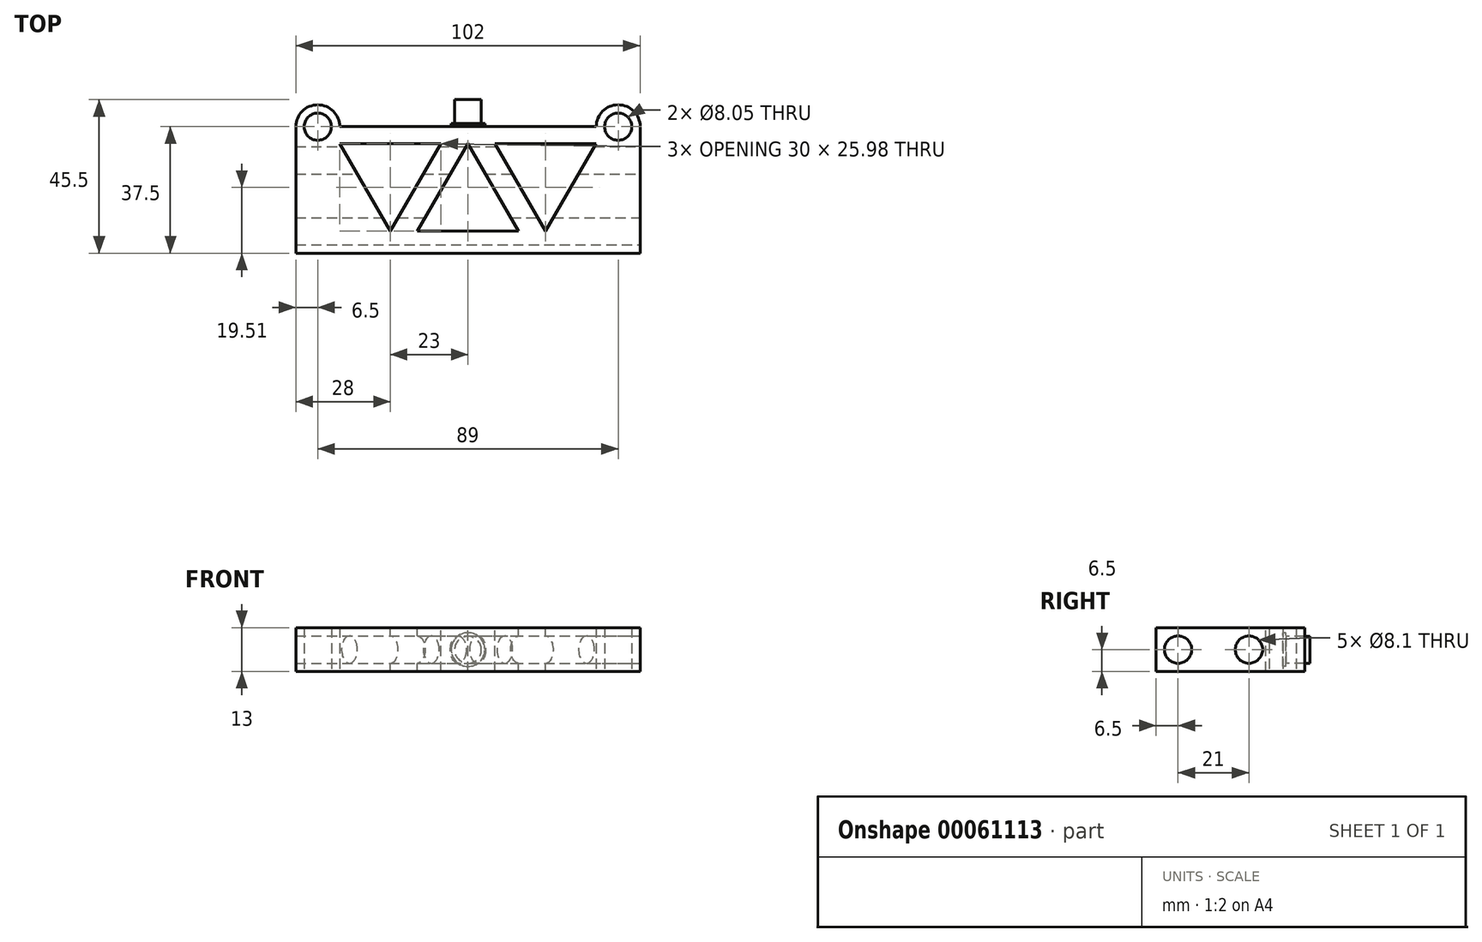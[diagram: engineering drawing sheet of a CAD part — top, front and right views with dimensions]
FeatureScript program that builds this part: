
annotation { "Feature Type Name" : "Feature", "Feature Type Description" : "" }
export const myFeature = defineFeature(function(context is Context, id is Id, definition is map)
    precondition{}
    {
        {
            var Q0;
            Q0=qCreatedBy(makeId("Top.planeOp"),FACE);
            var sketch = newSketch(context, id + "F0", { "sketchPlane" : qUnion([Q0])});
            skLineSegment(sketch, "E0", {"start": v(0, 0) * mm, "end": v(-38, 0) * mm});
            skLineSegment(sketch, "E1", {"start": v(0, 0) * mm, "end": v(38, 0) * mm});
            skCircle(sketch, "E2", {"center": v(-44.5, 0) * mm, "radius": 4.03 * mm});
            skCircle(sketch, "E3", {"center": v(44.5, 0) * mm, "radius": 4.03 * mm});
            skArc(sketch, "E4", {"start": v(-38, 0) * mm, "mid": v(-44.5, 6.5) * mm, "end": v(-51, 0) * mm});
            skArc(sketch, "E5", {"start": v(51, 0) * mm, "mid": v(44.5, 6.5) * mm, "end": v(38, 0) * mm});
            skLineSegment(sketch, "E6", {"start": v(0, 0) * mm, "end": v(0, -37.5) * mm, "construction": true});
            skLineSegment(sketch, "E7", {"start": v(0, -37.5) * mm, "end": v(-51, -37.5) * mm});
            skLineSegment(sketch, "E8", {"start": v(0, -37.5) * mm, "end": v(51, -37.5) * mm});
            skLineSegment(sketch, "E9", {"start": v(-51, -37.5) * mm, "end": v(-51, 0) * mm});
            skLineSegment(sketch, "E10", {"start": v(51, -37.5) * mm, "end": v(51, 0) * mm});
            skSolve(sketch);
        }
        {
            var Q0;
            Q0=makeQuery(id+"F0.imprint","IMPRINT",FACE,{"disambiguationData":[TD([[makeQuery(id+"F0.imprint","IMPRINT",EDGE,{"derivedFrom":sQuery(id+"F0.wireOp",EDGE,"E0")}),1.0]])]});
            extrude(context, id + "F1", {"entities" : qUnion([Q0]), "depth" : 13 * mm});
        }
        {
            var Q0;
            Q0=makeQuery(id+"F1.opExtrude","SWEPT_FACE",FACE,{"disambiguationData":[OSD([sQuery(id+"F0.wireOp",EDGE,"E10")])]});
            var sketch = newSketch(context, id + "F2", { "sketchPlane" : qUnion([Q0])});
            skLineSegment(sketch, "E11", {"start": v(0, 6.5) * mm, "end": v(-10, 6.5) * mm, "construction": true});
            skCircle(sketch, "E12", {"center": v(-10, 6.5) * mm, "radius": 4.05 * mm});
            skLineSegment(sketch, "E13", {"start": v(-10, 6.5) * mm, "end": v(-31, 6.5) * mm, "construction": true});
            skCircle(sketch, "E14", {"center": v(-31, 6.5) * mm, "radius": 4.05 * mm});
            skSolve(sketch);
        }
        {
            var Q0;
            Q0=makeQuery(id+"F2.imprint","IMPRINT",FACE,{"disambiguationData":[TD([[makeQuery(id+"F2.imprint","IMPRINT",EDGE,{"derivedFrom":sQuery(id+"F2.wireOp",EDGE,"E12")}),1.0]])]});
            var Q1;
            Q1=makeQuery(id+"F2.imprint","IMPRINT",FACE,{"disambiguationData":[TD([[makeQuery(id+"F2.imprint","IMPRINT",EDGE,{"derivedFrom":sQuery(id+"F2.wireOp",EDGE,"E14")}),1.0]])]});
            extrude(context, id + "F3", {"entities" : qUnion([Q0, Q1]), "operationType" : NewBodyOperationType.REMOVE, "oppositeDirection" : true, "depth" : 200 * mm});
        }
        {
            var Q0;
            Q0=makeQuery(id+"F1.opExtrude","CAP_FACE",FACE,{"disambiguationData":[OSD([sQuery(id+"F0.wireOp",EDGE,"E0"),sQuery(id+"F0.wireOp",EDGE,"E1"),sQuery(id+"F0.wireOp",EDGE,"E2"),sQuery(id+"F0.wireOp",EDGE,"E3"),sQuery(id+"F0.wireOp",EDGE,"E4"),sQuery(id+"F0.wireOp",EDGE,"E5"),sQuery(id+"F0.wireOp",EDGE,"E7"),sQuery(id+"F0.wireOp",EDGE,"E8"),sQuery(id+"F0.wireOp",EDGE,"E9"),sQuery(id+"F0.wireOp",EDGE,"E10")])],"isStart":false});
            var sketch = newSketch(context, id + "F4", { "sketchPlane" : qUnion([Q0])});
            skLineSegment(sketch, "E15", {"start": v(-8, -5) * mm, "end": v(-38, -5) * mm});
            skLineSegment(sketch, "E16", {"start": v(-38, -5) * mm, "end": v(-23, -30.98) * mm});
            skLineSegment(sketch, "E17", {"start": v(-23, -30.98) * mm, "end": v(-8, -5) * mm});
            skLineSegment(sketch, "E18", {"start": v(-38, 0) * mm, "end": v(-38, -5) * mm, "construction": true});
            skLineSegment(sketch, "E19", {"start": v(38, 0) * mm, "end": v(38, -5) * mm, "construction": true});
            skLineSegment(sketch, "E20", {"start": v(38, -5) * mm, "end": v(8, -5) * mm});
            skLineSegment(sketch, "E21", {"start": v(8, -5) * mm, "end": v(23, -30.98) * mm});
            skLineSegment(sketch, "E22", {"start": v(23, -30.98) * mm, "end": v(38, -5) * mm});
            skLineSegment(sketch, "E23", {"start": v(0, -5) * mm, "end": v(-15, -30.98) * mm});
            skLineSegment(sketch, "E24", {"start": v(-15, -30.98) * mm, "end": v(15, -30.98) * mm});
            skLineSegment(sketch, "E25", {"start": v(15, -30.98) * mm, "end": v(0, -5) * mm});
            skSolve(sketch);
        }
        {
            var Q0;
            Q0=makeQuery(id+"F4.imprint","IMPRINT",FACE,{"disambiguationData":[TD([[makeQuery(id+"F4.imprint","IMPRINT",EDGE,{"derivedFrom":sQuery(id+"F4.wireOp",EDGE,"E15")}),1.0]])]});
            var Q1;
            Q1=makeQuery(id+"F4.imprint","IMPRINT",FACE,{"disambiguationData":[TD([[makeQuery(id+"F4.imprint","IMPRINT",EDGE,{"derivedFrom":sQuery(id+"F4.wireOp",EDGE,"E23")}),1.0]])]});
            var Q2;
            Q2=makeQuery(id+"F4.imprint","IMPRINT",FACE,{"disambiguationData":[TD([[makeQuery(id+"F4.imprint","IMPRINT",EDGE,{"derivedFrom":sQuery(id+"F4.wireOp",EDGE,"E20")}),1.0]])]});
            extrude(context, id + "F5", {"entities" : qUnion([Q0, Q1, Q2]), "operationType" : NewBodyOperationType.REMOVE, "oppositeDirection" : true, "depth" : 25 * mm});
        }
        {
            var Q0;
            Q0=makeQuery(id+"F1.opExtrude","SWEPT_FACE",FACE,{"disambiguationData":[OSD([sQuery(id+"F0.wireOp",EDGE,"E0"),sQuery(id+"F0.wireOp",EDGE,"E1")])]});
            var sketch = newSketch(context, id + "F6", { "sketchPlane" : qUnion([Q0])});
            skLineSegment(sketch, "E26", {"start": v(0, 0) * mm, "end": v(0, 6.5) * mm, "construction": true});
            skCircle(sketch, "E27", {"center": v(0, 6.5) * mm, "radius": 5 * mm});
            skCircle(sketch, "E28", {"center": v(0, 6.45) * mm, "radius": 3.98 * mm});
            skSolve(sketch);
        }
        {
            var Q0;
            Q0 = qSketchRegion(id + "F6", true);
            extrude(context, id + "F7", {"entities" : qUnion([Q0]), "operationType" : NewBodyOperationType.ADD, "depth" : 1 * mm});
        }
        {
            var Q0;
            Q0=makeQuery(id+"F6.imprint","IMPRINT",FACE,{"disambiguationData":[TD([[makeQuery(id+"F6.imprint","IMPRINT",EDGE,{"derivedFrom":sQuery(id+"F6.wireOp",EDGE,"E28")}),1.0]])]});
            extrude(context, id + "F8", {"entities" : qUnion([Q0]), "operationType" : NewBodyOperationType.ADD, "depth" : 8 * mm});
        }
    });
